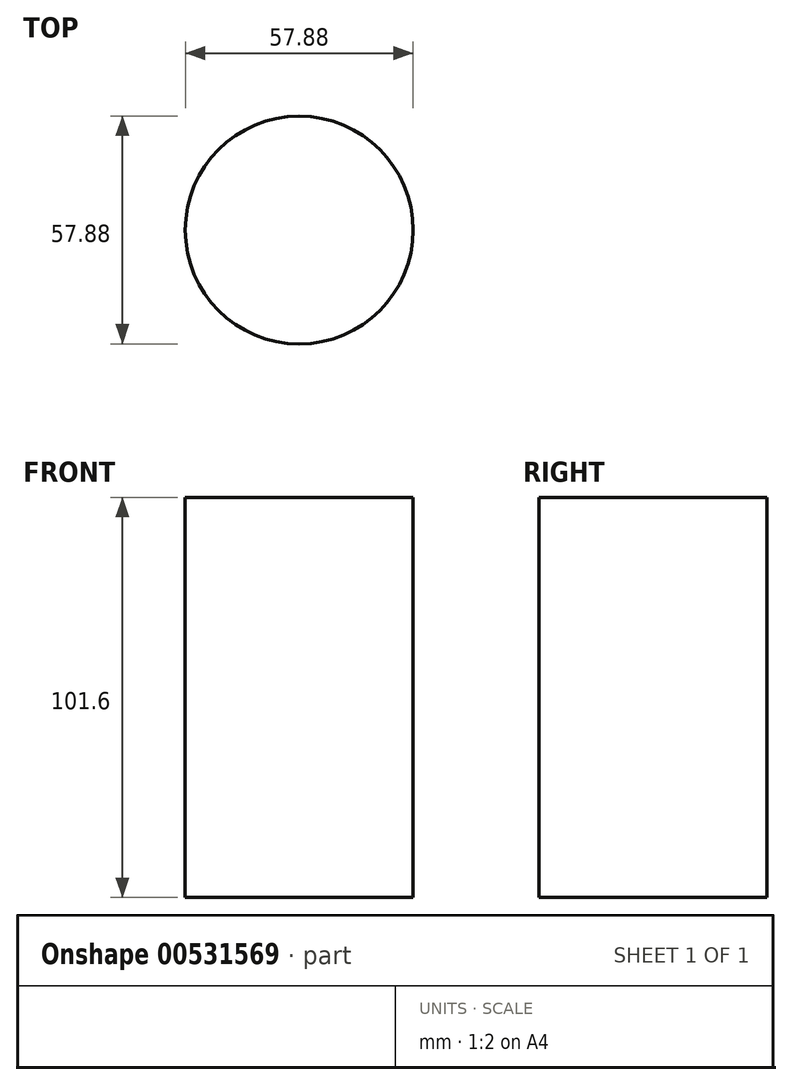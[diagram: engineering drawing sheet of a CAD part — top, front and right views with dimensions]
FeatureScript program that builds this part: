
annotation { "Feature Type Name" : "Feature", "Feature Type Description" : "" }
export const myFeature = defineFeature(function(context is Context, id is Id, definition is map)
    precondition{}
    {
        {
            var Q0;
            Q0=qCreatedBy(makeId("Top.planeOp"),FACE);
            var sketch = newSketch(context, id + "F0", { "sketchPlane" : qUnion([Q0])});
            skCircle(sketch, "E0", {"center": v(-1.99, 0) * mm, "radius": 28.94 * mm});
            skSolve(sketch);
        }
        {
            var Q0;
            Q0 = qSketchRegion(id + "F0", true);
            extrude(context, id + "F1", {"entities" : qUnion([Q0]), "depth" : 101.6 * mm, "offsetDistance" : 25.4 * mm});
        }
    });
